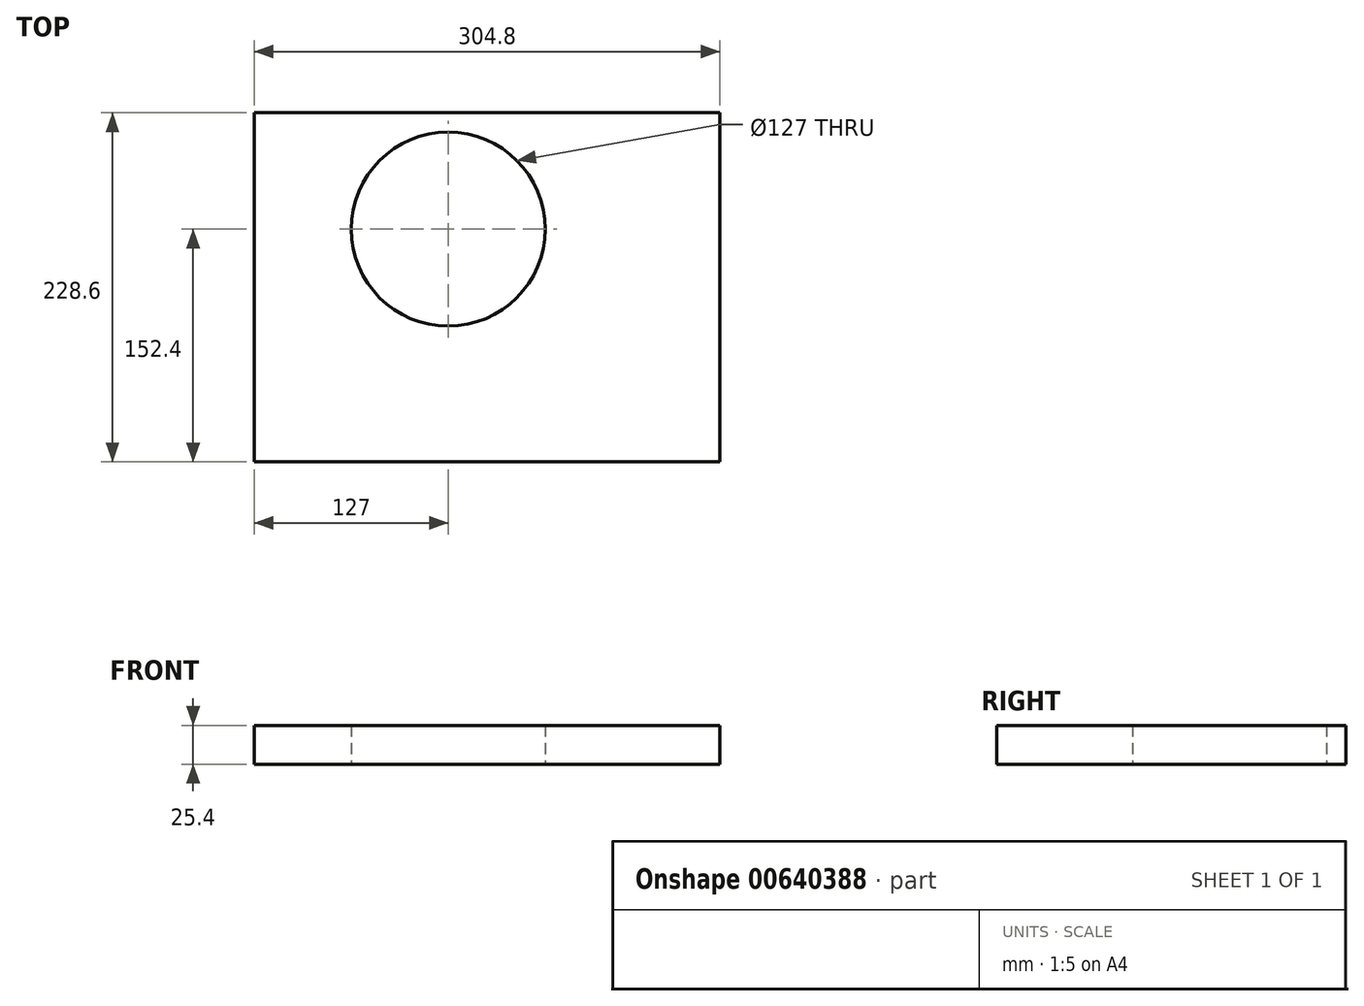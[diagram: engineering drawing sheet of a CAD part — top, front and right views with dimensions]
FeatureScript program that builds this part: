
annotation { "Feature Type Name" : "Feature", "Feature Type Description" : "" }
export const myFeature = defineFeature(function(context is Context, id is Id, definition is map)
    precondition{}
    {
        {
            var Q0;
            Q0=qCreatedBy(makeId("Top.planeOp"),FACE);
            var sketch = newSketch(context, id + "F0", { "sketchPlane" : qUnion([Q0])});
            skLineSegment(sketch, "E0.bottom", {"start": v(0, 0) * mm, "end": v(304.8, 0) * mm});
            skLineSegment(sketch, "E0.top", {"start": v(0, 228.6) * mm, "end": v(304.8, 228.6) * mm});
            skLineSegment(sketch, "E0.left", {"start": v(0, 0) * mm, "end": v(0, 228.6) * mm});
            skLineSegment(sketch, "E0.right", {"start": v(304.8, 0) * mm, "end": v(304.8, 228.6) * mm});
            skCircle(sketch, "E1", {"center": v(127, 152.4) * mm, "radius": 63.5 * mm});
            skSolve(sketch);
        }
        {
            var Q0;
            Q0=makeQuery(id+"F0.imprint","IMPRINT",FACE,{"disambiguationData":[TD([[makeQuery(id+"F0.imprint","IMPRINT",EDGE,{"derivedFrom":sQuery(id+"F0.wireOp",EDGE,"E0.bottom")}),1.0]])]});
            extrude(context, id + "F1", {"entities" : qUnion([Q0]), "endBound" : BoundingType.SYMMETRIC, "depth" : 25.4 * mm, "offsetDistance" : 25.4 * mm});
        }
    });
